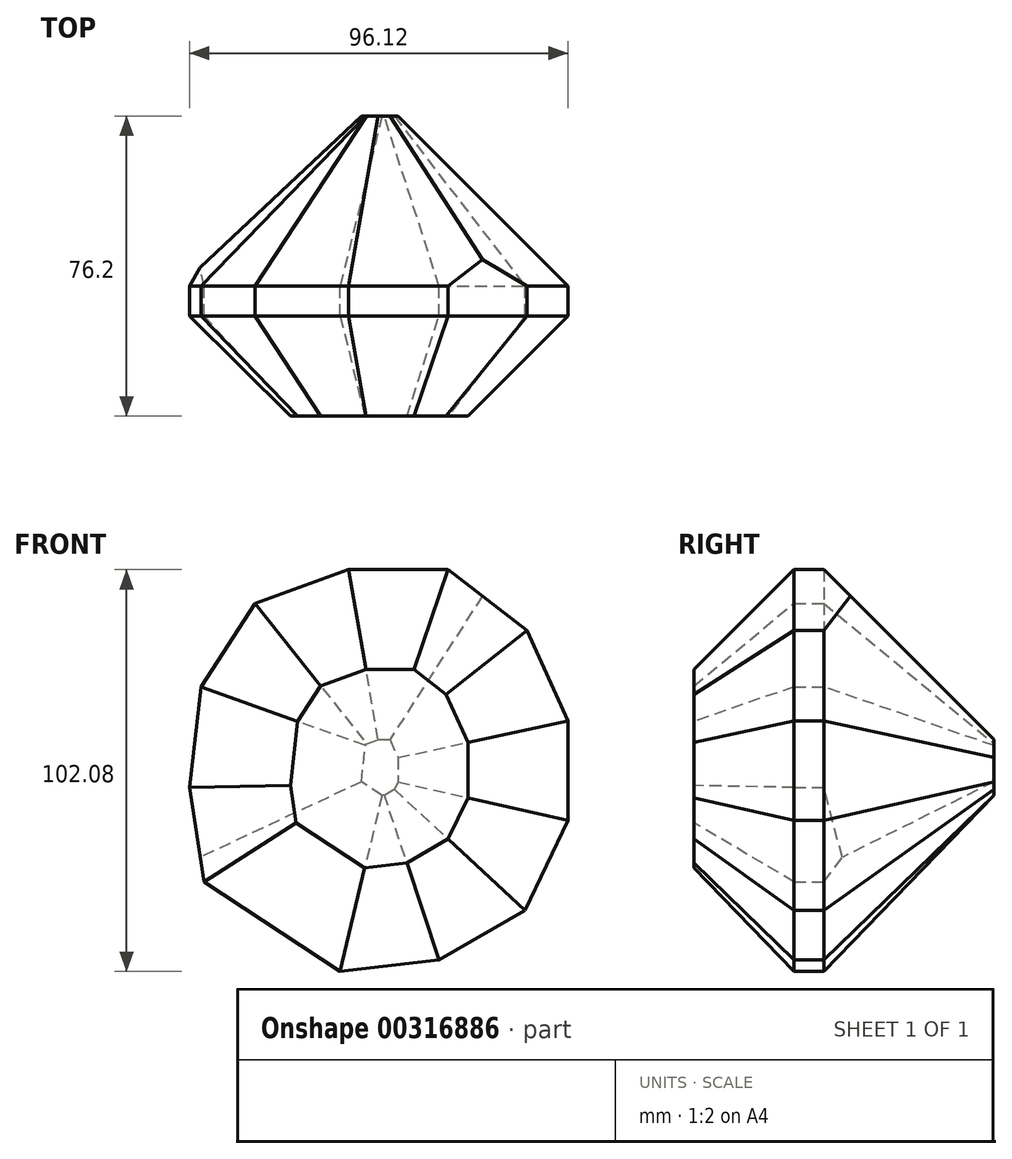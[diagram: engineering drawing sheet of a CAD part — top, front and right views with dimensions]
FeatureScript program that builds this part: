
annotation { "Feature Type Name" : "Feature", "Feature Type Description" : "" }
export const myFeature = defineFeature(function(context is Context, id is Id, definition is map)
    precondition{}
    {
        {
            var Q0;
            Q0=qCreatedBy(makeId("Front.planeOp"),FACE);
            var sketch = newSketch(context, id + "F0", { "sketchPlane" : qUnion([Q0])});
            skLineSegment(sketch, "E0", {"start": v(-46.76, 55.54) * mm, "end": v(-22.98, 64.1) * mm});
            skLineSegment(sketch, "E1", {"start": v(-22.98, 64.1) * mm, "end": v(2.3, 64.1) * mm});
            skLineSegment(sketch, "E2", {"start": v(2.3, 64.1) * mm, "end": v(22.34, 48.7) * mm});
            skLineSegment(sketch, "E3", {"start": v(-46.76, 55.54) * mm, "end": v(-60.47, 34.3) * mm});
            skLineSegment(sketch, "E4", {"start": v(-25.11, -37.98) * mm, "end": v(0, -35.09) * mm});
            skLineSegment(sketch, "E5", {"start": v(0, -35.09) * mm, "end": v(21.88, -22.43) * mm});
            skLineSegment(sketch, "E6", {"start": v(21.88, -22.43) * mm, "end": v(32.76, 0.39) * mm});
            skLineSegment(sketch, "E7", {"start": v(32.76, 0.39) * mm, "end": v(32.76, 25.66) * mm});
            skLineSegment(sketch, "E8", {"start": v(32.76, 25.66) * mm, "end": v(22.34, 48.7) * mm});
            skLineSegment(sketch, "E9", {"start": v(-60.47, 34.3) * mm, "end": v(-63.36, 8.72) * mm});
            skLineSegment(sketch, "E10", {"start": v(-63.36, 8.72) * mm, "end": v(-59.72, -15.23) * mm});
            skLineSegment(sketch, "E11", {"start": v(-59.72, -15.23) * mm, "end": v(-25.11, -37.98) * mm});
            skSolve(sketch);
        }
        {
            var Q0;
            Q0 = qSketchRegion(id + "F0", true);
            extrude(context, id + "F1", {"entities" : qUnion([Q0]), "depth" : 76.2 * mm});
        }
        {
            var Q0;
            Q0=makeQuery(id+"F1.opExtrude","CAP_EDGE",EDGE,{"disambiguationData":[OSD([sQuery(id+"F0.wireOp",EDGE,"E10")])],"isStart":false});
            var Q1;
            Q1=makeQuery(id+"F1.opExtrude","CAP_EDGE",EDGE,{"disambiguationData":[OSD([sQuery(id+"F0.wireOp",EDGE,"E11")])],"isStart":false});
            var Q2;
            Q2=makeQuery(id+"F1.opExtrude","CAP_EDGE",EDGE,{"disambiguationData":[OSD([sQuery(id+"F0.wireOp",EDGE,"E4")])],"isStart":false});
            var Q3;
            Q3=makeQuery(id+"F1.opExtrude","CAP_EDGE",EDGE,{"disambiguationData":[OSD([sQuery(id+"F0.wireOp",EDGE,"E5")])],"isStart":false});
            var Q4;
            Q4=makeQuery(id+"F1.opExtrude","CAP_EDGE",EDGE,{"disambiguationData":[OSD([sQuery(id+"F0.wireOp",EDGE,"E6")])],"isStart":false});
            var Q5;
            Q5=makeQuery(id+"F1.opExtrude","CAP_EDGE",EDGE,{"disambiguationData":[OSD([sQuery(id+"F0.wireOp",EDGE,"E7")])],"isStart":false});
            var Q6;
            Q6=makeQuery(id+"F1.opExtrude","CAP_EDGE",EDGE,{"disambiguationData":[OSD([sQuery(id+"F0.wireOp",EDGE,"E8")])],"isStart":false});
            var Q7;
            Q7=makeQuery(id+"F1.opExtrude","CAP_EDGE",EDGE,{"disambiguationData":[OSD([sQuery(id+"F0.wireOp",EDGE,"E2")])],"isStart":false});
            var Q8;
            Q8=makeQuery(id+"F1.opExtrude","CAP_EDGE",EDGE,{"disambiguationData":[OSD([sQuery(id+"F0.wireOp",EDGE,"E1")])],"isStart":false});
            var Q9;
            Q9=makeQuery(id+"F1.opExtrude","CAP_EDGE",EDGE,{"disambiguationData":[OSD([sQuery(id+"F0.wireOp",EDGE,"E0")])],"isStart":false});
            var Q10;
            Q10=makeQuery(id+"F1.opExtrude","CAP_EDGE",EDGE,{"disambiguationData":[OSD([sQuery(id+"F0.wireOp",EDGE,"E3")])],"isStart":false});
            var Q11;
            Q11=makeQuery(id+"F1.opExtrude","CAP_EDGE",EDGE,{"disambiguationData":[OSD([sQuery(id+"F0.wireOp",EDGE,"E9")])],"isStart":false});
            chamfer(context, id + "F2", {"entities" : qUnion([Q0, Q1, Q2, Q3, Q4, Q5, Q6, Q7, Q8, Q9, Q10, Q11]), "width" : 25.4 * mm, "tangentPropagation" : true});
        }
        {
            var Q0;
            Q0=makeQuery(id+"F1.opExtrude","CAP_FACE",FACE,{"disambiguationData":[OSD([sQuery(id+"F0.wireOp",EDGE,"E0"),sQuery(id+"F0.wireOp",EDGE,"E1"),sQuery(id+"F0.wireOp",EDGE,"E2"),sQuery(id+"F0.wireOp",EDGE,"E3"),sQuery(id+"F0.wireOp",EDGE,"E4"),sQuery(id+"F0.wireOp",EDGE,"E5"),sQuery(id+"F0.wireOp",EDGE,"E6"),sQuery(id+"F0.wireOp",EDGE,"E7"),sQuery(id+"F0.wireOp",EDGE,"E8"),sQuery(id+"F0.wireOp",EDGE,"E9"),sQuery(id+"F0.wireOp",EDGE,"E10"),sQuery(id+"F0.wireOp",EDGE,"E11")])],"isStart":true});
            chamfer(context, id + "F3", {"entities" : qUnion([Q0]), "width" : 43.18 * mm, "tangentPropagation" : true});
        }
    });
